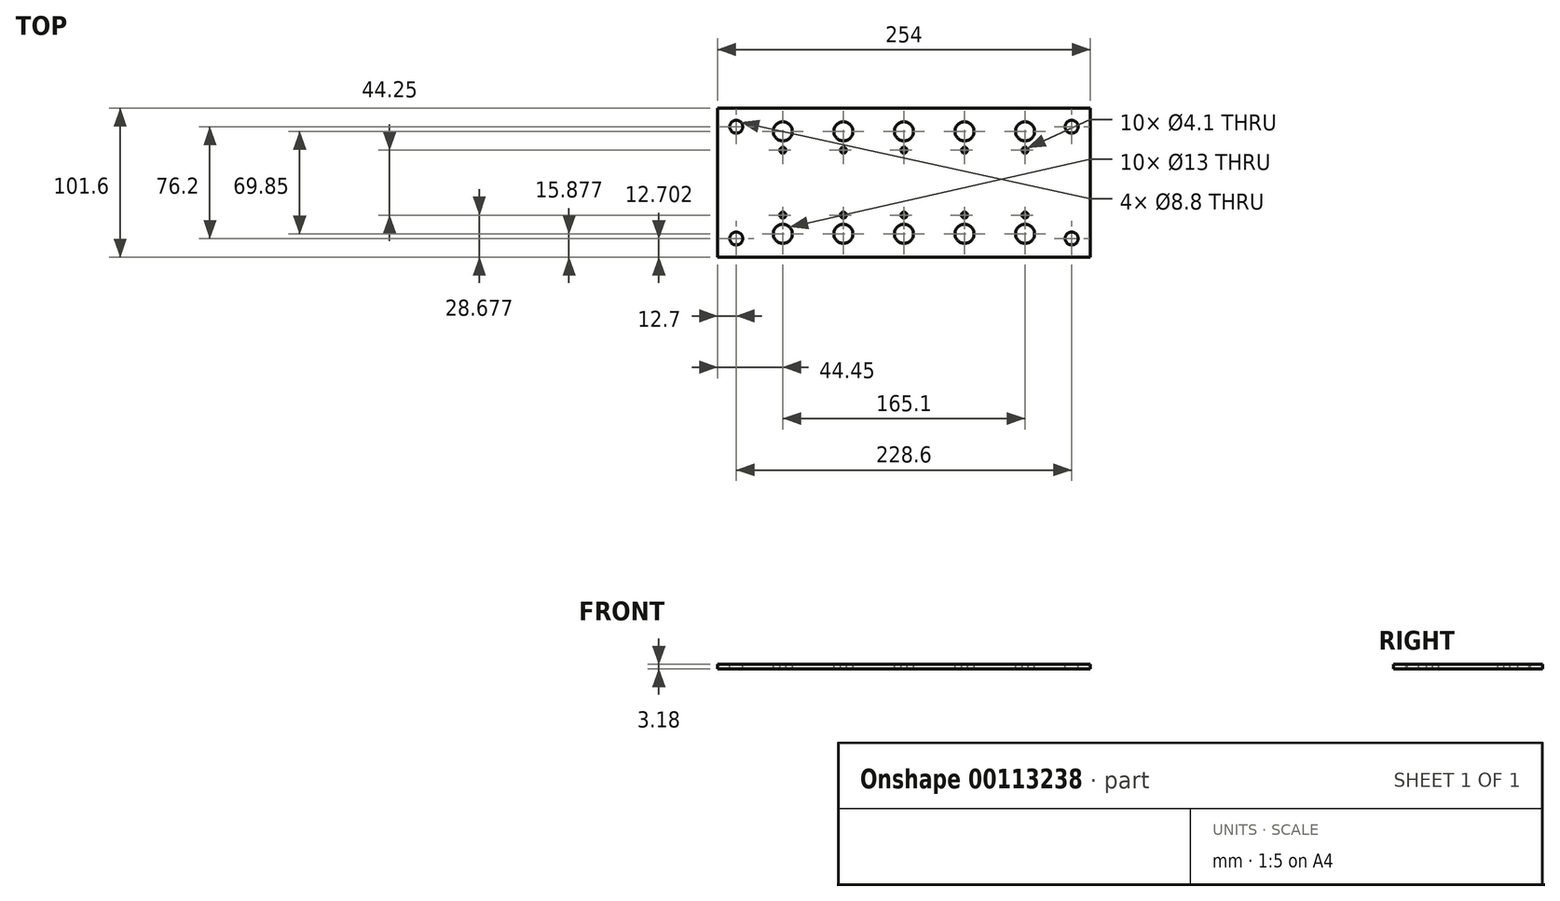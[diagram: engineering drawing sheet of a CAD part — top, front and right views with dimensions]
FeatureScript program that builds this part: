
annotation { "Feature Type Name" : "Feature", "Feature Type Description" : "" }
export const myFeature = defineFeature(function(context is Context, id is Id, definition is map)
    precondition{}
    {
        {
            var Q0;
            Q0=qCreatedBy(makeId("Top.planeOp"),FACE);
            var sketch = newSketch(context, id + "F0", { "sketchPlane" : qUnion([Q0])});
            skLineSegment(sketch, "E0.bottom", {"start": v(-102.08, 88.55) * mm, "end": v(177.32, 88.55) * mm});
            skLineSegment(sketch, "E0.top", {"start": v(-102.08, -13.05) * mm, "end": v(177.32, -13.05) * mm});
            skLineSegment(sketch, "E0.left", {"start": v(-102.08, 88.55) * mm, "end": v(-102.08, -13.05) * mm});
            skLineSegment(sketch, "E0.right", {"start": v(177.32, 88.55) * mm, "end": v(177.32, -13.05) * mm});
            skSolve(sketch);
        }
        {
            var Q0;
            Q0=makeQuery(id+"F0.imprint","IMPRINT",FACE,{"disambiguationData":[TD([[makeQuery(id+"F0.imprint","IMPRINT",EDGE,{"derivedFrom":sQuery(id+"F0.wireOp",EDGE,"E0.bottom")}),-1.0]])]});
            extrude(context, id + "F1", {"entities" : qUnion([Q0]), "depth" : 3.17 * mm});
        }
        {
            var Q0;
            Q0=makeQuery(id+"F1.opExtrude","CAP_FACE",FACE,{"disambiguationData":[OSD([sQuery(id+"F0.wireOp",EDGE,"E0.bottom"),sQuery(id+"F0.wireOp",EDGE,"E0.top"),sQuery(id+"F0.wireOp",EDGE,"E0.left"),sQuery(id+"F0.wireOp",EDGE,"E0.right")])],"isStart":false});
            var sketch = newSketch(context, id + "F2", { "sketchPlane" : qUnion([Q0])});
            skLineSegment(sketch, "E1", {"start": v(-102.08, 63.15) * mm, "end": v(-76.68, 63.15) * mm});
            skLineSegment(sketch, "E2", {"start": v(-76.68, 63.15) * mm, "end": v(-76.68, -13.05) * mm});
            skSolve(sketch);
        }
        {
            var Q0;
            {var subQ0=sQuery(id+"F2.wireOp",EDGE,"E1");Q0=makeQuery(id+"F2.imprint","IMPRINT",FACE,{"disambiguationData":[TD([[makeQuery(id+"F2.imprint","IMPRINT",EDGE,{"derivedFrom":subQ0}),-1.0]])]});}
            extrude(context, id + "F3", {"entities" : qUnion([Q0]), "operationType" : NewBodyOperationType.REMOVE, "endBound" : BoundingType.THROUGH_ALL, "oppositeDirection" : true, "depth" : 25.4 * mm});
        }
        {
            var Q0;
            {var subQ0=sQuery(id+"F0.wireOp",EDGE,"E0.right");var subQ1=sQuery(id+"F0.wireOp",EDGE,"E0.left");var subQ2=sQuery(id+"F0.wireOp",EDGE,"E0.top");var subQ3=sQuery(id+"F0.wireOp",EDGE,"E0.bottom");Q0=makeQuery(id+"FE4L4fvrKudPUKG_1.boolean.opBoolean","MERGE",FACE,{"derivedFrom":[makeQuery(id+"F1.opExtrude","CAP_FACE",FACE,{"disambiguationData":[OSD([subQ3,subQ2,subQ1,subQ0])],"isStart":false}),makeQuery(id+"FE4L4fvrKudPUKG_1.opExtrude","CAP_FACE",FACE,{"disambiguationData":[OSD([subQ3,subQ2,subQ1,subQ0,sQuery(id+"F2.wireOp",EDGE,"E1"),sQuery(id+"F2.wireOp",EDGE,"E2"),sQuery(id+"FlZwbx96tAhKAK0_1.wireOp",EDGE,"fe8319e8-427f-4688-8bb2-b74819dc0c91.top"),sQuery(id+"FlZwbx96tAhKAK0_1.wireOp",EDGE,"fe8319e8-427f-4688-8bb2-b74819dc0c91.left"),sQuery(id+"FlZwbx96tAhKAK0_1.wireOp",EDGE,"fe8319e8-427f-4688-8bb2-b74819dc0c91.right")])],"isStart":false})]});}
            var sketch = newSketch(context, id + "F4", { "sketchPlane" : qUnion([Q0])});
            skPoint(sketch, "E3", {"position": v(-89.38, 75.85) * mm});
            skSolve(sketch);
        }
        {
            var Q0;
            Q0=sQuery(id+"F4.wireOp",VERTEX,"E3");
            var Q1;
            Q1=makeQuery(id+"F1.opExtrude","SWEPT_BODY",BODY,{"disambiguationData":[OSD([sQuery(id+"F0.wireOp",EDGE,"E0.bottom"),sQuery(id+"F0.wireOp",EDGE,"E0.top"),sQuery(id+"F0.wireOp",EDGE,"E0.left"),sQuery(id+"F0.wireOp",EDGE,"E0.right")])]});
            hole(context, id + "F5", {"style" : HoleStyle.SIMPLE, "endStyle" : HoleEndStyle.THROUGH, "holeDiameter" : 6.35 * mm, "locations" : qUnion([Q0]), "scope" : qUnion([Q1]), "isTappedThrough" : true});
        }
        {
            var Q0;
            {var subQ0=sQuery(id+"F0.wireOp",EDGE,"E0.right");var subQ1=sQuery(id+"F0.wireOp",EDGE,"E0.left");var subQ2=sQuery(id+"F0.wireOp",EDGE,"E0.top");var subQ3=sQuery(id+"F0.wireOp",EDGE,"E0.bottom");Q0=makeQuery(id+"FE4L4fvrKudPUKG_1.boolean.opBoolean","MERGE",FACE,{"derivedFrom":[makeQuery(id+"F1.opExtrude","CAP_FACE",FACE,{"disambiguationData":[OSD([subQ3,subQ2,subQ1,subQ0])],"isStart":false}),makeQuery(id+"FE4L4fvrKudPUKG_1.opExtrude","CAP_FACE",FACE,{"disambiguationData":[OSD([subQ3,subQ2,subQ1,subQ0,sQuery(id+"F2.wireOp",EDGE,"E1"),sQuery(id+"F2.wireOp",EDGE,"E2"),sQuery(id+"FlZwbx96tAhKAK0_1.wireOp",EDGE,"fe8319e8-427f-4688-8bb2-b74819dc0c91.top"),sQuery(id+"FlZwbx96tAhKAK0_1.wireOp",EDGE,"fe8319e8-427f-4688-8bb2-b74819dc0c91.left"),sQuery(id+"FlZwbx96tAhKAK0_1.wireOp",EDGE,"fe8319e8-427f-4688-8bb2-b74819dc0c91.right")])],"isStart":false})]});}
            var sketch = newSketch(context, id + "F6", { "sketchPlane" : qUnion([Q0])});
            skPoint(sketch, "E4", {"position": v(-63.98, 75.85) * mm});
            skSolve(sketch);
        }
        {
            var Q0;
            Q0=sQuery(id+"F6.wireOp",VERTEX,"E4");
            var Q1;
            Q1=makeQuery(id+"F1.opExtrude","SWEPT_BODY",BODY,{"disambiguationData":[OSD([sQuery(id+"F0.wireOp",EDGE,"E0.bottom"),sQuery(id+"F0.wireOp",EDGE,"E0.top"),sQuery(id+"F0.wireOp",EDGE,"E0.left"),sQuery(id+"F0.wireOp",EDGE,"E0.right")])]});
            hole(context, id + "F7", {"style" : HoleStyle.SIMPLE, "endStyle" : HoleEndStyle.THROUGH, "standardTappedOrClearance" : lookupTablePath({ "standard" : "ISO", "fit" : "Normal", "size" : "M8", "type" : "Clearance" }), "standardBlindInLast" : lookupTablePath({ "fit" : "Standard", "standard" : "ISO", "size" : "M8", "type" : "Clearance" }), "holeDiameter" : 8.8 * mm, "locations" : qUnion([Q0]), "scope" : qUnion([Q1]), "isTappedThrough" : true});
        }
        {
            var Q0;
            {var subQ0=sQuery(id+"F0.wireOp",EDGE,"E0.right");var subQ1=sQuery(id+"F0.wireOp",EDGE,"E0.left");var subQ2=sQuery(id+"F0.wireOp",EDGE,"E0.top");var subQ3=sQuery(id+"F0.wireOp",EDGE,"E0.bottom");Q0=makeQuery(id+"FE4L4fvrKudPUKG_1.boolean.opBoolean","MERGE",FACE,{"derivedFrom":[makeQuery(id+"F1.opExtrude","CAP_FACE",FACE,{"disambiguationData":[OSD([subQ3,subQ2,subQ1,subQ0])],"isStart":false}),makeQuery(id+"FE4L4fvrKudPUKG_1.opExtrude","CAP_FACE",FACE,{"disambiguationData":[OSD([subQ3,subQ2,subQ1,subQ0,sQuery(id+"F2.wireOp",EDGE,"E1"),sQuery(id+"F2.wireOp",EDGE,"E2"),sQuery(id+"FlZwbx96tAhKAK0_1.wireOp",EDGE,"fe8319e8-427f-4688-8bb2-b74819dc0c91.top"),sQuery(id+"FlZwbx96tAhKAK0_1.wireOp",EDGE,"fe8319e8-427f-4688-8bb2-b74819dc0c91.left"),sQuery(id+"FlZwbx96tAhKAK0_1.wireOp",EDGE,"fe8319e8-427f-4688-8bb2-b74819dc0c91.right")])],"isStart":false})]});}
            var sketch = newSketch(context, id + "F8", { "sketchPlane" : qUnion([Q0])});
            skLineSegment(sketch, "E5", {"start": v(50.32, 88.55) * mm, "end": v(50.32, -13.05) * mm, "construction": true});
            skLineSegment(sketch, "E6", {"start": v(50.32, 37.75) * mm, "end": v(-76.68, 37.75) * mm, "construction": true});
            skLineSegment(sketch, "E7", {"start": v(50.32, 37.75) * mm, "end": v(177.32, 37.75) * mm, "construction": true});
            skCircle(sketch, "E8.0", {"center": v(-63.98, 75.85) * mm, "radius": 4.4 * mm, "construction": true});
            skCircle(sketch, "E9.MirrorC", {"center": v(-63.98, -0.35) * mm, "radius": 4.4 * mm, "construction": true});
            skCircle(sketch, "E10.MirrorC", {"center": v(164.62, 75.85) * mm, "radius": 4.4 * mm, "construction": true});
            skCircle(sketch, "E11.MirrorC", {"center": v(164.62, -0.35) * mm, "radius": 4.4 * mm, "construction": true});
            skSolve(sketch);
        }
        {
            var Q0;
            Q0=sQuery(id+"F8.wireOp",VERTEX,"E9.MirrorC.center");
            var Q1;
            Q1=sQuery(id+"F8.wireOp",VERTEX,"E11.MirrorC.center");
            var Q2;
            Q2=sQuery(id+"F8.wireOp",VERTEX,"E10.MirrorC.center");
            var Q3;
            Q3=makeQuery(id+"F1.opExtrude","SWEPT_BODY",BODY,{"disambiguationData":[OSD([sQuery(id+"F0.wireOp",EDGE,"E0.bottom"),sQuery(id+"F0.wireOp",EDGE,"E0.top"),sQuery(id+"F0.wireOp",EDGE,"E0.left"),sQuery(id+"F0.wireOp",EDGE,"E0.right")])]});
            hole(context, id + "F9", {"style" : HoleStyle.SIMPLE, "endStyle" : HoleEndStyle.THROUGH, "standardTappedOrClearance" : lookupTablePath({ "standard" : "ISO", "fit" : "Normal", "size" : "M8", "type" : "Clearance" }), "standardBlindInLast" : lookupTablePath({ "fit" : "Standard", "standard" : "ISO", "size" : "M8", "type" : "Clearance" }), "holeDiameter" : 8.8 * mm, "locations" : qUnion([Q0, Q1, Q2]), "scope" : qUnion([Q3]), "isTappedThrough" : true});
        }
        {
            var Q0;
            {var subQ0=sQuery(id+"F0.wireOp",EDGE,"E0.right");var subQ1=sQuery(id+"F0.wireOp",EDGE,"E0.left");var subQ2=sQuery(id+"F0.wireOp",EDGE,"E0.top");var subQ3=sQuery(id+"F0.wireOp",EDGE,"E0.bottom");Q0=makeQuery(id+"FihavrzHuo13blj_1.boolean.opBoolean","MERGE",FACE,{"derivedFrom":[makeQuery(id+"FE4L4fvrKudPUKG_1.boolean.opBoolean","MERGE",FACE,{"derivedFrom":[makeQuery(id+"F1.opExtrude","CAP_FACE",FACE,{"disambiguationData":[OSD([subQ3,subQ2,subQ1,subQ0])],"isStart":false}),makeQuery(id+"FE4L4fvrKudPUKG_1.opExtrude","CAP_FACE",FACE,{"disambiguationData":[OSD([subQ3,subQ2,subQ1,subQ0,sQuery(id+"F2.wireOp",EDGE,"E1"),sQuery(id+"F2.wireOp",EDGE,"E2"),sQuery(id+"FlZwbx96tAhKAK0_1.wireOp",EDGE,"fe8319e8-427f-4688-8bb2-b74819dc0c91.top"),sQuery(id+"FlZwbx96tAhKAK0_1.wireOp",EDGE,"fe8319e8-427f-4688-8bb2-b74819dc0c91.left"),sQuery(id+"FlZwbx96tAhKAK0_1.wireOp",EDGE,"fe8319e8-427f-4688-8bb2-b74819dc0c91.right")])],"isStart":false})]}),makeQuery(id+"FihavrzHuo13blj_1.opExtrude","SWEPT_FACE",FACE,{"disambiguationData":[OSD([sQuery(id+"FqzX0JU06Psa10b_1.wireOp",EDGE,"pASvYPJX-orRT-4wvN-Okg9-zyxHxzA8P6ji.top")])]})]});}
            var sketch = newSketch(context, id + "F10", { "sketchPlane" : qUnion([Q0])});
            skCircle(sketch, "E12.0", {"center": v(-63.98, 75.85) * mm, "radius": 4.4 * mm});
            skCircle(sketch, "E13.0", {"center": v(164.62, 75.85) * mm, "radius": 4.4 * mm});
            skLineSegment(sketch, "E14", {"start": v(-76.68, 72.68) * mm, "end": v(-32.23, 72.68) * mm, "construction": true});
            skLineSegment(sketch, "E15", {"start": v(-32.23, 72.68) * mm, "end": v(9.04, 72.68) * mm, "construction": true});
            skLineSegment(sketch, "E16", {"start": v(9.04, 72.68) * mm, "end": v(50.32, 72.68) * mm, "construction": true});
            skLineSegment(sketch, "E17", {"start": v(50.32, 72.68) * mm, "end": v(91.6, 72.68) * mm, "construction": true});
            skLineSegment(sketch, "E18", {"start": v(91.6, 72.68) * mm, "end": v(132.87, 72.68) * mm, "construction": true});
            skLineSegment(sketch, "E19", {"start": v(132.87, 72.68) * mm, "end": v(177.32, 72.68) * mm, "construction": true});
            skPoint(sketch, "E20", {"position": v(-32.23, 72.68) * mm});
            skPoint(sketch, "E21", {"position": v(9.04, 72.68) * mm});
            skPoint(sketch, "E22", {"position": v(50.32, 72.68) * mm});
            skPoint(sketch, "E23", {"position": v(91.6, 72.68) * mm});
            skPoint(sketch, "E24", {"position": v(132.87, 72.68) * mm});
            skPoint(sketch, "E25", {"position": v(-32.23, 59.88) * mm});
            skPoint(sketch, "E26", {"position": v(9.04, 59.88) * mm});
            skPoint(sketch, "E27", {"position": v(50.32, 59.88) * mm});
            skPoint(sketch, "E28", {"position": v(91.6, 59.88) * mm});
            skPoint(sketch, "E29", {"position": v(132.87, 59.88) * mm});
            skPoint(sketch, "E30", {"position": v(-32.23, 15.63) * mm});
            skPoint(sketch, "E31", {"position": v(9.04, 15.63) * mm});
            skPoint(sketch, "E32", {"position": v(50.32, 15.63) * mm});
            skPoint(sketch, "E33", {"position": v(91.6, 15.63) * mm});
            skPoint(sketch, "E34", {"position": v(132.87, 15.63) * mm});
            skPoint(sketch, "E35", {"position": v(-32.23, 2.83) * mm});
            skPoint(sketch, "E36", {"position": v(9.04, 2.83) * mm});
            skPoint(sketch, "E37", {"position": v(50.32, 2.83) * mm});
            skPoint(sketch, "E38", {"position": v(91.6, 2.83) * mm});
            skPoint(sketch, "E39", {"position": v(132.87, 2.83) * mm});
            skLineSegment(sketch, "E40", {"start": v(-32.23, 2.83) * mm, "end": v(-32.23, 15.63) * mm, "construction": true});
            skLineSegment(sketch, "E41", {"start": v(-32.23, 59.88) * mm, "end": v(-32.23, 72.68) * mm, "construction": true});
            skLineSegment(sketch, "E42", {"start": v(50.32, 2.83) * mm, "end": v(50.32, -13.05) * mm, "construction": true});
            skLineSegment(sketch, "E43", {"start": v(50.32, 72.68) * mm, "end": v(50.32, 88.55) * mm, "construction": true});
            skSolve(sketch);
        }
        {
            var Q0;
            Q0=sQuery(id+"F10.wireOp",VERTEX,"E34");
            var Q1;
            Q1=sQuery(id+"F10.wireOp",VERTEX,"E33");
            var Q2;
            Q2=sQuery(id+"F10.wireOp",VERTEX,"E32");
            var Q3;
            Q3=sQuery(id+"F10.wireOp",VERTEX,"E31");
            var Q4;
            Q4=sQuery(id+"F10.wireOp",VERTEX,"E30");
            var Q5;
            Q5=sQuery(id+"F10.wireOp",VERTEX,"E29");
            var Q6;
            Q6=sQuery(id+"F10.wireOp",VERTEX,"E28");
            var Q7;
            Q7=sQuery(id+"F10.wireOp",VERTEX,"E27");
            var Q8;
            Q8=sQuery(id+"F10.wireOp",VERTEX,"E26");
            var Q9;
            Q9=sQuery(id+"F10.wireOp",VERTEX,"E25");
            var Q10;
            Q10=makeQuery(id+"F1.opExtrude","SWEPT_BODY",BODY,{"disambiguationData":[OSD([sQuery(id+"F0.wireOp",EDGE,"E0.bottom"),sQuery(id+"F0.wireOp",EDGE,"E0.top"),sQuery(id+"F0.wireOp",EDGE,"E0.left"),sQuery(id+"F0.wireOp",EDGE,"E0.right")])]});
            hole(context, id + "F11", {"style" : HoleStyle.SIMPLE, "endStyle" : HoleEndStyle.THROUGH, "standardTappedOrClearance" : lookupTablePath({ "standard" : "ISO", "engagement" : "75%", "pitch" : "0.9 mm", "size" : "M5", "type" : "Tapped" }), "standardBlindInLast" : lookupTablePath({ "standard" : "ISO", "engagement" : "75%", "pitch" : "0.9 mm", "size" : "M5", "type" : "Tapped" }), "holeDiameter" : 4.1 * mm, "locations" : qUnion([Q0, Q1, Q2, Q3, Q4, Q5, Q6, Q7, Q8, Q9]), "scope" : qUnion([Q10]), "isTappedThrough" : true, "showTappedDepth" : true});
        }
        {
            var Q0;
            Q0=makeQuery(id+"F1.opExtrude","CAP_FACE",FACE,{"disambiguationData":[OSD([sQuery(id+"F0.wireOp",EDGE,"E0.bottom"),sQuery(id+"F0.wireOp",EDGE,"E0.top"),sQuery(id+"F0.wireOp",EDGE,"E0.left"),sQuery(id+"F0.wireOp",EDGE,"E0.right")])],"isStart":false});
            var sketch = newSketch(context, id + "F12", { "sketchPlane" : qUnion([Q0])});
            skLineSegment(sketch, "E44.bottom", {"start": v(-76.68, 63.15) * mm, "end": v(-102.08, 63.15) * mm});
            skLineSegment(sketch, "E44.top", {"start": v(-76.68, 88.55) * mm, "end": v(-102.08, 88.55) * mm});
            skLineSegment(sketch, "E44.left", {"start": v(-76.68, 63.15) * mm, "end": v(-76.68, 88.55) * mm});
            skLineSegment(sketch, "E44.right", {"start": v(-102.08, 63.15) * mm, "end": v(-102.08, 88.55) * mm});
            skSolve(sketch);
        }
        {
            var Q0;
            Q0=makeQuery(id+"F12.imprint","IMPRINT",FACE,{"disambiguationData":[TD([[makeQuery(id+"F12.imprint","IMPRINT",EDGE,{"derivedFrom":sQuery(id+"F12.wireOp",EDGE,"E44.bottom")}),1.0]])]});
            extrude(context, id + "F13", {"entities" : qUnion([Q0]), "operationType" : NewBodyOperationType.REMOVE, "oppositeDirection" : true, "depth" : 25.4 * mm});
        }
        {
            var Q0;
            Q0=sQuery(id+"F10.wireOp",VERTEX,"E39");
            var Q1;
            Q1=sQuery(id+"F10.wireOp",VERTEX,"E38");
            var Q2;
            Q2=sQuery(id+"F10.wireOp",VERTEX,"E37");
            var Q3;
            Q3=sQuery(id+"F10.wireOp",VERTEX,"E36");
            var Q4;
            Q4=sQuery(id+"F10.wireOp",VERTEX,"E35");
            var Q5;
            Q5=sQuery(id+"F10.wireOp",VERTEX,"E24");
            var Q6;
            Q6=sQuery(id+"F10.wireOp",VERTEX,"E23");
            var Q7;
            Q7=sQuery(id+"F10.wireOp",VERTEX,"E22");
            var Q8;
            Q8=sQuery(id+"F10.wireOp",VERTEX,"E21");
            var Q9;
            Q9=sQuery(id+"F10.wireOp",VERTEX,"E20");
            var Q10;
            Q10=makeQuery(id+"F1.opExtrude","SWEPT_BODY",BODY,{"disambiguationData":[OSD([sQuery(id+"F0.wireOp",EDGE,"E0.bottom"),sQuery(id+"F0.wireOp",EDGE,"E0.top"),sQuery(id+"F0.wireOp",EDGE,"E0.left"),sQuery(id+"F0.wireOp",EDGE,"E0.right")])]});
            hole(context, id + "F14", {"style" : HoleStyle.SIMPLE, "endStyle" : HoleEndStyle.THROUGH, "holeDiameter" : 13 * mm, "locations" : qUnion([Q0, Q1, Q2, Q3, Q4, Q5, Q6, Q7, Q8, Q9]), "scope" : qUnion([Q10]), "isTappedThrough" : true});
        }
    });
